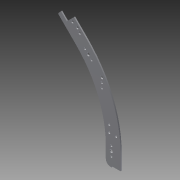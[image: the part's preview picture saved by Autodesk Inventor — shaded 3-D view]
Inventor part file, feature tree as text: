
AUTODESK INVENTOR PART (.ipt)
format: ipt  version: 2014 SP1 (Build 180222100, 222)  size: 169,472 bytes
history: native  units: in
note: dims shown in document units (in); Inventor stores cm internally (conversion verified against a paired STEP export)
features: extrude x1, sketch x1
ambient origin geometry x8: Origin, YZ Plane, XZ Plane, XY Plane, X Axis, Y Axis, Z Axis, Center Point
bodies: Solid1 (feature_tree)
feature tree (2):
  extrude  "Extrusion1"  Depth=12.5876in
  sketch  "Sketch1"  dims[d0=11.0in d1=12.5876in d2=0.266in d3=0.266in d4=0.266in d5=0.2244in d6=0.3268in d7=0.2244in d8=0.315in d9=0.2244in d10=0.2244in d11=0.125in d12=0.5in d13=0.875in d14=1.0876in d15=1.8824in d16=2.7574in d17=2.6324in d18=45.0deg d19=0.266in d20=0.266in d21=0.266in d22=0.224in d23=0.3268in d24=0.224in d25=0.5in d26=0.12in d27=0.9675in d28=0.125in d29=1.6324in d30=1.2574in d32=0.5803in d33=0.875in d34=1.3676in d35=0.75in d36=0.75in d37=0.3376in d38=0.4399in d39=6.7416in d40=0.747in d41=2.5in d42=0.25in d43=0.5in d44=0.336in d46=0.8243in d48=1.0in d49=1.0in d50=1.0in d51=0.125in d52=0.0in d53=0.25in d54=0.375in]
